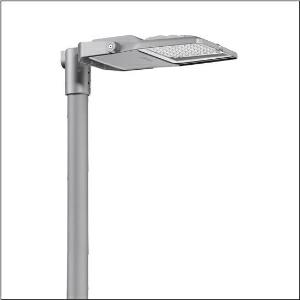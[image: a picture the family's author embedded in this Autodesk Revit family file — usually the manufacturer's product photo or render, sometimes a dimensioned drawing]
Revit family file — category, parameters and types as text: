
# Revit family: floodlight_fl_21_iq_mini___pl43_5xa7771c4a3a_be4f
name_source: partatom
category: Lighting Fixtures
units: mm (PartAtom-declared; Revit-internal decimal feet)

## family parameters
Cut with Voids When Loaded = No
Host = Face
Light Source = No
Part Type = Normal
Room Calculation Point = No
Round Connector Dimension = Use Diameter
Shared = No

## types (1)
- --- (1 x LED, 13050 lm, 87.2 W, 4000K)
    Apparent Load = 87 VA
    CIE Flux Codes = 27 78 99 100 100
    Color Rendering = 70
    Color Temperature = 4000K
    Default Elevation = 1800 mm
    Description = Floodlight FL 21 iQ mini, floodlight, primary light control with lens, of PMMA, primary optical cover: protective disc, of toughened safety glass, transparent, light distribution: PL43, light emission: direct distribution, installation type: surface-mounted, LED, High Power LED, rated luminous flux: 13.050lm, luminous efficacy: 150lm/W, light colour: 740, colour temperature: 4000K, control: Auto-Match, Temp-Guard, Lumen-Switch, Night-Set, Smart-Wire, Light-Fading, Desk-Remote (wireless, voltage-free reading and setting of iQ features in the workshop via application-optimized NFC function/RFID function), optimised constant luminous flux control (CLO 2.0), with terminal, 6-pole, mains connection: 220..240V, AC, 50/60Hz, start of lifetime: 87W, end of service life: 92W, reduction: 40W, luminaire housing, of diecast aluminium, powder-coated, Siteco® metallic grey (DB 702S), corrosivity category C5 mid according to DIN EN ISO 12944, sealing non-destructively replaceable, please order mast flange separately, mast bracket, of steel, galvanised, powder-coated, Siteco® metallic grey (DB 702S), protection rating (complete): IP66, insulation class (complete): insulation class II (safety insulation), certification: CE, ENEC, VDE, protection symbol: D, impact resistance: IK08, permissible operating ambient temperature: -40..+40°C, permissible operating ambient temperature for outdoor applications: -40..+50°C, standard: DIN EN 12944, LABS conformity tested according to VDMA 24364:2018-05, packaging unit: 1 piece

Light Distribution: PL43
    Height = 70 mm
    Lamp = 1 x LED
    Lamp Light Flux = 13050 lm
    Lamp Power = 87.2 W
    Lamp count = 1
    Length = 485 mm
    Luminous efficacy = 150 lm/W
    Manufacturer = Siteco
    ModVariant = No
    Model = 5XA7771C4A3A
    Number of Poles = 1
    OnlyDefault = Yes
    Power Factor = 1
    Product Name = Floodlight FL 21 iQ mini | PL43
    Product group = floodlight | pylon annexe
    ProductGroupID = 6200
    Protection Class = Protection class II
    Protection Degree = IP 66
    RLX_Detail_Level = 1
    RLX_Emergency_Light_Flux = 0 lm
    RLX_Emergency_Type = 0
    RLX_Emergency_Type_DB = No
    RlxData = <blob elided: 101245 chars, md5=c2cebd8f>
    Socket = socket
    Standby Power = 0 W
    System Light Flux = 13050 lm
    System Power = 87 W
    Type Comments = factory setting: luminous flux: 100 % | dim-lin: 254 | 456 mA
    Type Image = l_1007125.jpg
    URL = http://relux.com
    VarID = @adj_112581
    Voltage = 0 V
    Weight = 0.00 kg
    Width = 337 mm

## geometry (parser evidence)
native form markers: Blend x4, Sweep x13
no freeform markers — native parametric forms only
